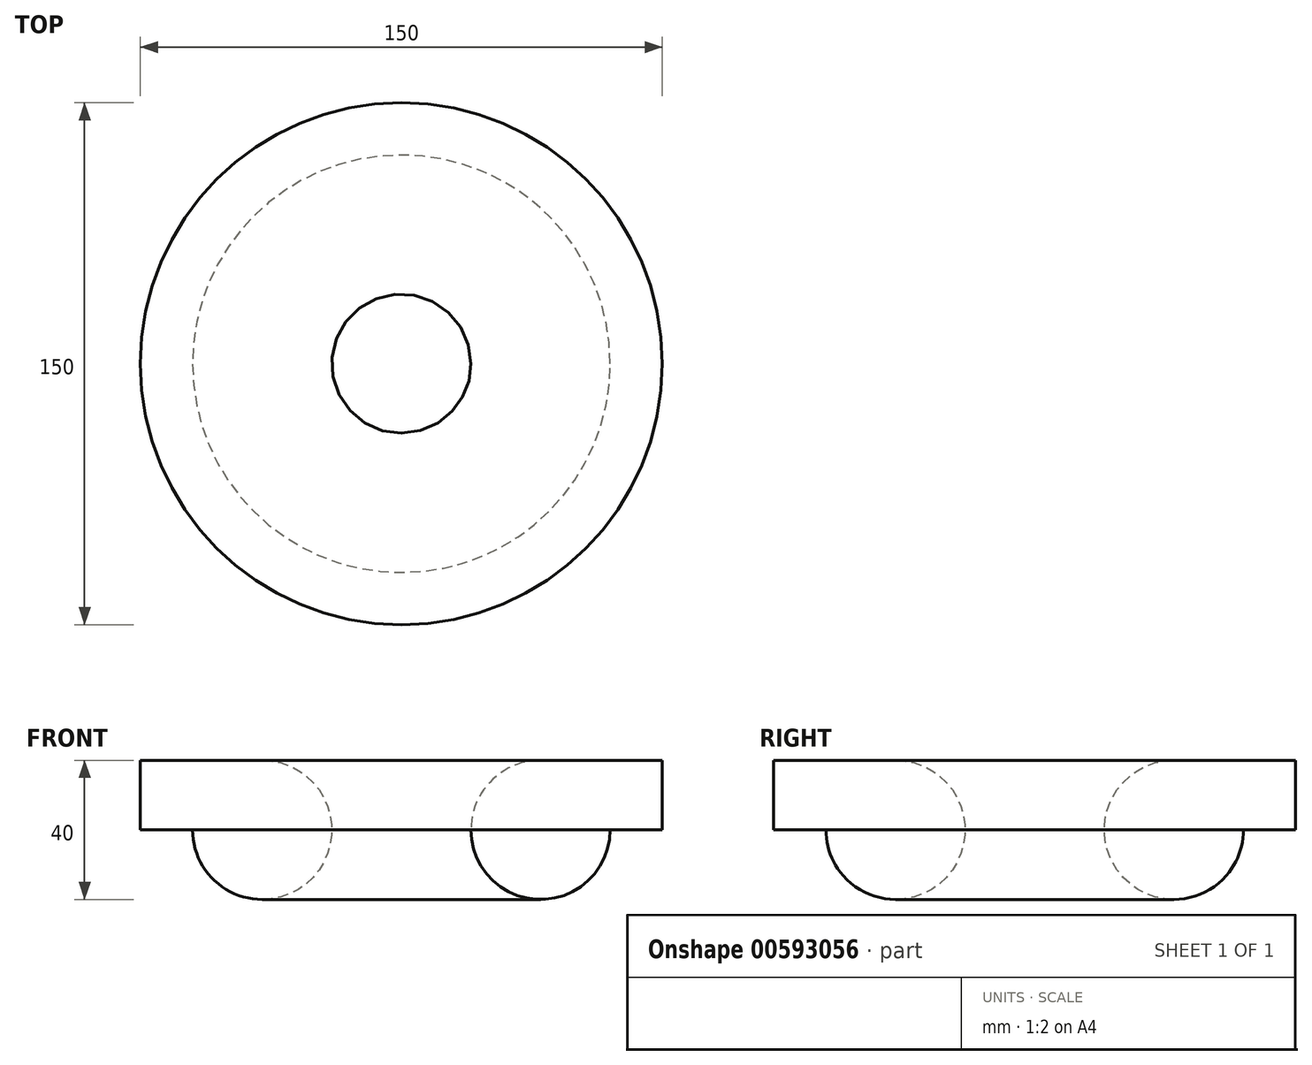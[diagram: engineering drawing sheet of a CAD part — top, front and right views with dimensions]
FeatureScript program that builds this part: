
annotation { "Feature Type Name" : "Feature", "Feature Type Description" : "" }
export const myFeature = defineFeature(function(context is Context, id is Id, definition is map)
    precondition{}
    {
        {
            var Q0;
            Q0=qCreatedBy(makeId("Front.planeOp"),FACE);
            var sketch = newSketch(context, id + "F0", { "sketchPlane" : qUnion([Q0])});
            skCircle(sketch, "E0", {"center": v(40, 0) * mm, "radius": 20 * mm});
            skLineSegment(sketch, "E1", {"start": v(0, 74.6) * mm, "end": v(0, -73.88) * mm, "construction": true});
            skLineSegment(sketch, "E2.bottom", {"start": v(40, 0) * mm, "end": v(75, 0) * mm});
            skLineSegment(sketch, "E2.top", {"start": v(40, 20) * mm, "end": v(75, 20) * mm});
            skLineSegment(sketch, "E2.left", {"start": v(40, 0) * mm, "end": v(40, 20) * mm});
            skLineSegment(sketch, "E2.right", {"start": v(75, 0) * mm, "end": v(75, 20) * mm});
            skSolve(sketch);
        }
        {
            var Q0;
            Q0 = qSketchRegion(id + "F0", true);
            var Q1;
            Q1=sQuery(id+"F0.wireOp",EDGE,"E1");
            var Q2;
            Q2=sQuery(id+"F0.wireOp",EDGE,"E1");
            revolve(context, id + "F1", {"entities" : qUnion([Q0]), "surfaceEntities" : qUnion([Q1]), "axis" : qUnion([Q2]), "revolveType" : RevolveType.FULL});
        }
    });
